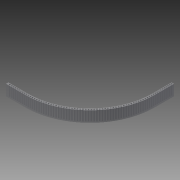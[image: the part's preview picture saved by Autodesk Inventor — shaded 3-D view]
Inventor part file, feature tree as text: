
AUTODESK INVENTOR PART (.ipt)
format: ipt  version: 2013 (Build 170138000, 138)  size: 194,048 bytes
history: native  units: in
note: dims shown in document units (in); Inventor stores cm internally (conversion verified against a paired STEP export)
features: extrude x1, sketch x1
ambient origin geometry x8: Origin, YZ Plane, XZ Plane, XY Plane, X Axis, Y Axis, Z Axis, Center Point
bodies: Solid1 (feature_tree)
feature tree (2):
  extrude  "Extrusion1"  Depth=27.0in
  sketch  "Sketch1"  dims[d0=26.0in d1=27.0in d2=4.0in d3=4.3307in d5=0.375in d6=0.3937in d8=1.0in d10=4.0in d11=9.8425in d13=0.2907in d15=9.8425in d17=0.2907in d19=3.5433in d21=0.375in d22=0.3937in d24=1.0in d26=2.25in d27=0.0in]
